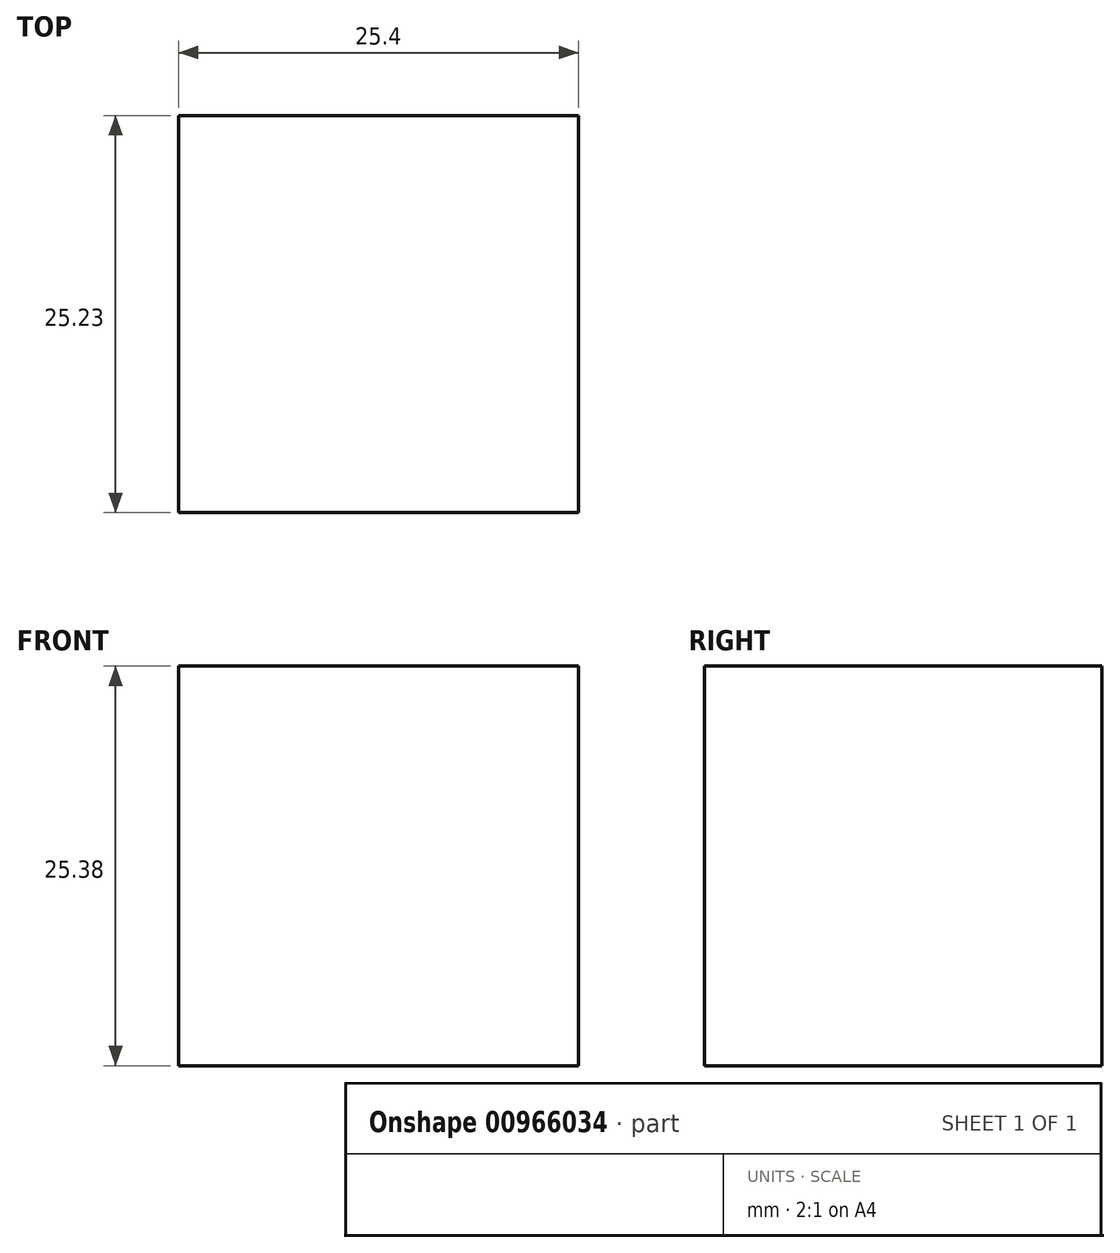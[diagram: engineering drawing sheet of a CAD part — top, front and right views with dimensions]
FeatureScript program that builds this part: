
annotation { "Feature Type Name" : "Feature", "Feature Type Description" : "" }
export const myFeature = defineFeature(function(context is Context, id is Id, definition is map)
    precondition{}
    {
        {
            var Q0;
            Q0=qCreatedBy(makeId("Right.planeOp"),FACE);
            var sketch = newSketch(context, id + "F0", { "sketchPlane" : qUnion([Q0])});
            skLineSegment(sketch, "E0", {"start": v(0, 0) * mm, "end": v(25.23, 0) * mm});
            skLineSegment(sketch, "E1", {"start": v(25.23, 0) * mm, "end": v(25.23, -25.38) * mm});
            skLineSegment(sketch, "E2", {"start": v(25.23, -25.38) * mm, "end": v(0, -25.38) * mm});
            skLineSegment(sketch, "E3", {"start": v(0, -25.38) * mm, "end": v(0, 0) * mm});
            skSolve(sketch);
        }
        {
            var Q0;
            Q0=makeQuery(id+"F0.imprint","IMPRINT",FACE,{"disambiguationData":[TD([[makeQuery(id+"F0.imprint","IMPRINT",EDGE,{"derivedFrom":sQuery(id+"F0.wireOp",EDGE,"E0")}),-1.0]])]});
            extrude(context, id + "F1", {"entities" : qUnion([Q0]), "depth" : 25.4 * mm, "offsetDistance" : 25.4 * mm});
        }
    });
